# Revit family: Outdoor-Kitchen-Cabinets_Kalamazoo_Corner-Fillers_Signature1
name_source: partatom
category: Specialty Equipment
revit_build: Autodesk Revit 2018 (Build: 20190510_1515(x64)
units: mm (PartAtom-declared; Revit-internal decimal feet)

## family parameters
Always vertical = Yes
Cut with Voids When Loaded = No
OmniClass Number = 23.40.40.11
OmniClass Title = Specialized Food Storage and Display Furnishings
Part Type = Normal
Room Calculation Point = No
Round Connector Dimension = Use Diameter
Shared = No
Work Plane-Based = No

## types (4) — shared parameters
Assembly Code = E1090310
Keynote = 11400
Manufacturer = Kalamazoo Outdoor Gourmet
Product Material = Kalamazoo - Stainless Steel - 304 OR 316L
Product data url = https://www.bimobject.com
URL = https://kalamazoogourmet.com
Ι_Gnrc Mdl Optn 01 = Extension : + 3/4"
Ι_Gnrc Mdl Optn 02 = Extension : - 3/4"

## per-type parameters (varying)
| type | CRNR | Depth | Description | FLR | K-45 | K-90 | Weight (lb) | Width |
| K-45-CRNR | 3" | 32" | Signature 45-Degree Blind Corner Unit | No | Yes | No | 200.00 lbf | 32" |
| K-BLND-CRNR-SQR | 6" | 36" | Signature 90-Degree Blind Corner Unit | No | No | Yes | 245.00 lbf | 36" |
| K-CRNRFLR-4X4 | 4" | 10 1/2" | Signature 4-Inch Inside Corner Filler | Yes | No | No | 20.00 lbf | 10 1/2" |
| K-CRNRFLR-6X6 | 6" | 12 1/2" | Signature 6-Inch Inside Corner Filler | Yes | No | No | 20.00 lbf | 12 1/2" |

note: column(s) folded — value = type name in every type: Model

## geometry (parser evidence)
native form markers: Sweep x9
no freeform markers — native parametric forms only
